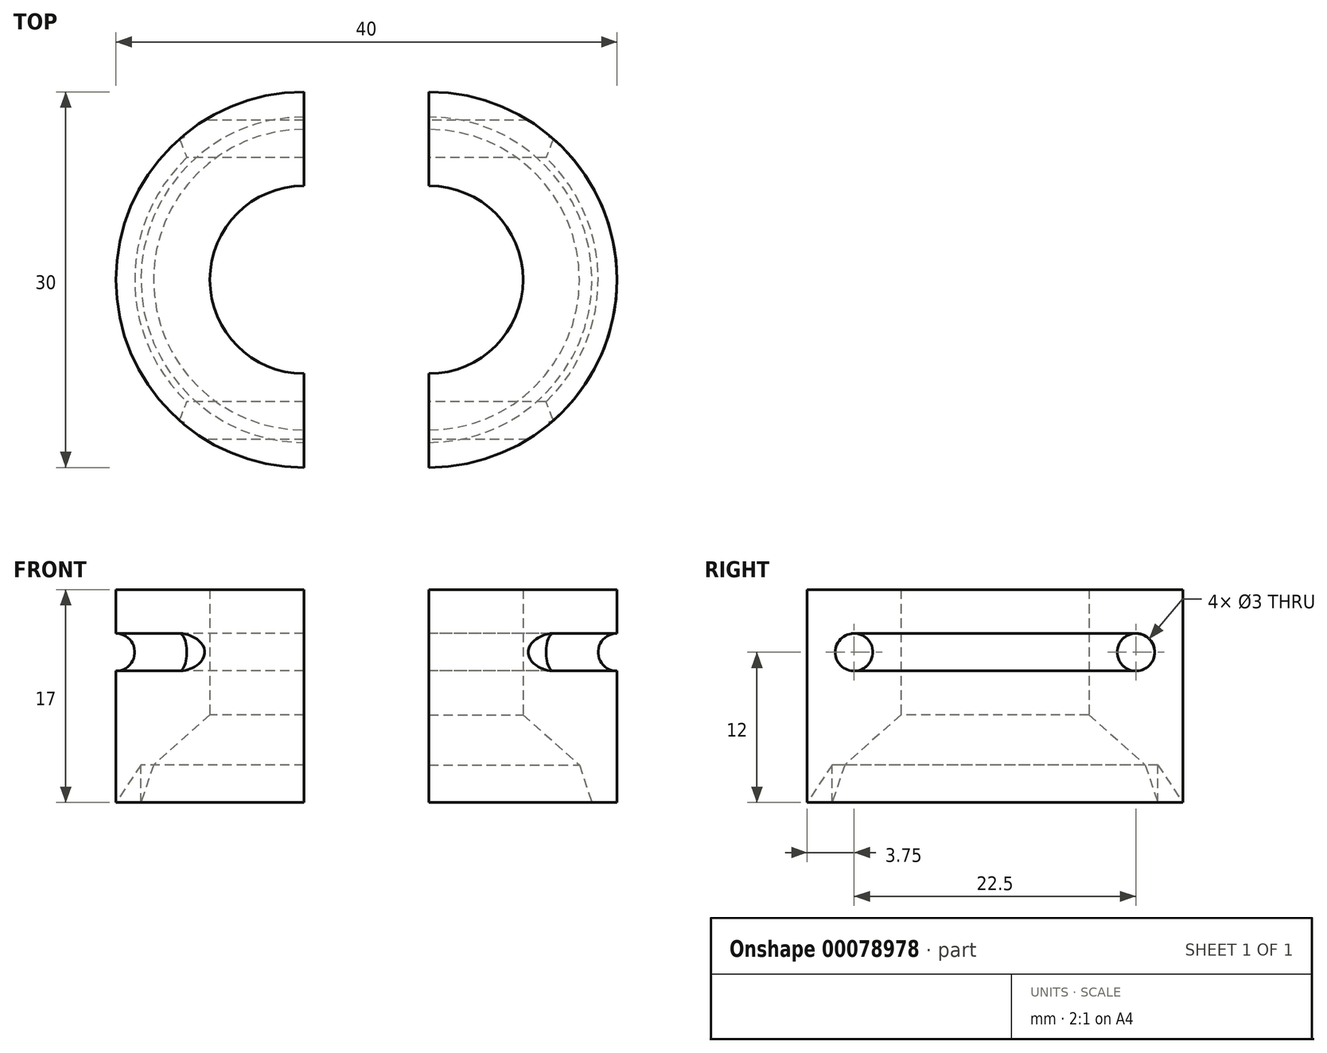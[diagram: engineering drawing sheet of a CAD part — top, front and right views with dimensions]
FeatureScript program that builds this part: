
annotation { "Feature Type Name" : "Feature", "Feature Type Description" : "" }
export const myFeature = defineFeature(function(context is Context, id is Id, definition is map)
    precondition{}
    {
        {
            var Q0;
            Q0=qCreatedBy(makeId("Top.planeOp"),FACE);
            var sketch = newSketch(context, id + "F0", { "sketchPlane" : qUnion([Q0])});
            skLineSegment(sketch, "E0", {"start": v(-10, 15) * mm, "end": v(-10, -15) * mm});
            skLineSegment(sketch, "E1", {"start": v(0, 15) * mm, "end": v(0, -15) * mm});
            skArc(sketch, "E2", {"start": v(-10, 15) * mm, "mid": v(-25, 0) * mm, "end": v(-10, -15) * mm});
            skArc(sketch, "E3", {"start": v(0, -15) * mm, "mid": v(15, 0) * mm, "end": v(0, 15) * mm});
            skArc(sketch, "E4", {"start": v(-10, 13) * mm, "mid": v(-23, 0) * mm, "end": v(-10, -13) * mm});
            skArc(sketch, "E5", {"start": v(0, -13) * mm, "mid": v(13, 0) * mm, "end": v(0, 13) * mm});
            skArc(sketch, "E6", {"start": v(0, -7.5) * mm, "mid": v(7.5, 0) * mm, "end": v(0, 7.5) * mm});
            skArc(sketch, "E7", {"start": v(-10, 7.5) * mm, "mid": v(-17.5, 0) * mm, "end": v(-10, -7.5) * mm});
            skArc(sketch, "E8", {"start": v(-10, 12) * mm, "mid": v(-22, 0) * mm, "end": v(-10, -12) * mm});
            skArc(sketch, "E9", {"start": v(0, -12) * mm, "mid": v(12, 0) * mm, "end": v(0, 12) * mm});
            skSolve(sketch);
        }
        {
            var Q0;
            {var subQ0=sQuery(id+"F0.wireOp",EDGE,"E4");Q0=makeQuery(id+"F0.imprint","IMPRINT",FACE,{"disambiguationData":[TD([[makeQuery(id+"F0.imprint","IMPRINT",EDGE,{"derivedFrom":subQ0}),1.0]])]});}
            var Q1;
            {var subQ0=sQuery(id+"F0.wireOp",EDGE,"E5");Q1=makeQuery(id+"F0.imprint","IMPRINT",FACE,{"disambiguationData":[TD([[makeQuery(id+"F0.imprint","IMPRINT",EDGE,{"derivedFrom":subQ0}),1.0]])]});}
            var Q2;
            {var subQ0=sQuery(id+"F0.wireOp",EDGE,"E7");Q2=makeQuery(id+"F0.imprint","IMPRINT",FACE,{"disambiguationData":[TD([[makeQuery(id+"F0.imprint","IMPRINT",EDGE,{"derivedFrom":subQ0}),-1.0]])]});}
            var Q3;
            {var subQ0=sQuery(id+"F0.wireOp",EDGE,"E6");Q3=makeQuery(id+"F0.imprint","IMPRINT",FACE,{"disambiguationData":[TD([[makeQuery(id+"F0.imprint","IMPRINT",EDGE,{"derivedFrom":subQ0}),-1.0]])]});}
            var Q4;
            {var subQ0=sQuery(id+"F0.wireOp",EDGE,"E2");Q4=makeQuery(id+"F0.imprint","IMPRINT",FACE,{"disambiguationData":[TD([[makeQuery(id+"F0.imprint","IMPRINT",EDGE,{"derivedFrom":subQ0}),1.0]])]});}
            var Q5;
            {var subQ0=sQuery(id+"F0.wireOp",EDGE,"E3");Q5=makeQuery(id+"F0.imprint","IMPRINT",FACE,{"disambiguationData":[TD([[makeQuery(id+"F0.imprint","IMPRINT",EDGE,{"derivedFrom":subQ0}),1.0]])]});}
            extrude(context, id + "F1", {"entities" : qUnion([Q0, Q1, Q2, Q3, Q4, Q5]), "depth" : 10 * mm});
        }
        {
            var Q0;
            {var subQ0=sQuery(id+"F0.wireOp",EDGE,"E1");var subQ2=makeQuery(id+"F0.imprint","INTERSECT",VERTEX,{"disambiguationData":[OD(1.0)],"derivedFrom":[subQ0,sQuery(id+"F0.wireOp",EDGE,"E5")]});Q0=makeQuery(id+"F1.opExtrude","SWEPT_FACE",FACE,{"disambiguationData":[OSD([subQ0]),TDD([makeQuery(id+"F0.imprint","IMPRINT",EDGE,{"disambiguationData":[TD([[makeQuery(id+"F0.imprint","INTERSECT",VERTEX,{"disambiguationData":[OD(0.0)],"derivedFrom":[subQ0,sQuery(id+"F0.wireOp",EDGE,"E3")]}),-1.0]])],"derivedFrom":subQ0}),makeQuery(id+"F0.imprint","IMPRINT",EDGE,{"disambiguationData":[TD([[subQ2,-1.0]])],"derivedFrom":subQ0}),makeQuery(id+"F0.imprint","IMPRINT",EDGE,{"disambiguationData":[TD([[makeQuery(id+"F0.imprint","INTERSECT",VERTEX,{"disambiguationData":[OD(1.0)],"derivedFrom":[subQ0,sQuery(id+"F0.wireOp",EDGE,"E6")]}),1.0]])],"derivedFrom":subQ0})])]});}
            var sketch = newSketch(context, id + "F2", { "sketchPlane" : qUnion([Q0])});
            skLineSegment(sketch, "E10", {"start": v(-11.25, 10) * mm, "end": v(-11.25, 0) * mm, "construction": true});
            skLineSegment(sketch, "E11", {"start": v(-15, 5) * mm, "end": v(-7.5, 5) * mm, "construction": true});
            skSolve(sketch);
        }
        {
            var Q0;
            {var subQ0=sQuery(id+"F0.wireOp",EDGE,"E1");var subQ1=makeQuery(id+"F0.imprint","INTERSECT",VERTEX,{"disambiguationData":[OD(0.0)],"derivedFrom":[subQ0,sQuery(id+"F0.wireOp",EDGE,"E5")]});Q0=makeQuery(id+"F1.opExtrude","SWEPT_FACE",FACE,{"disambiguationData":[OSD([subQ0]),TDD([makeQuery(id+"F0.imprint","IMPRINT",EDGE,{"disambiguationData":[TD([[makeQuery(id+"F0.imprint","INTERSECT",VERTEX,{"disambiguationData":[OD(0.0)],"derivedFrom":[subQ0,sQuery(id+"F0.wireOp",EDGE,"E6")]}),-1.0]])],"derivedFrom":subQ0}),makeQuery(id+"F0.imprint","IMPRINT",EDGE,{"disambiguationData":[TD([[subQ1,1.0]])],"derivedFrom":subQ0}),makeQuery(id+"F0.imprint","IMPRINT",EDGE,{"disambiguationData":[TD([[makeQuery(id+"F0.imprint","INTERSECT",VERTEX,{"disambiguationData":[OD(1.0)],"derivedFrom":[subQ0,sQuery(id+"F0.wireOp",EDGE,"E3")]}),1.0]])],"derivedFrom":subQ0})])]});}
            var sketch = newSketch(context, id + "F3", { "sketchPlane" : qUnion([Q0])});
            skLineSegment(sketch, "E12", {"start": v(11.25, 10) * mm, "end": v(11.25, 0) * mm, "construction": true});
            skLineSegment(sketch, "E13", {"start": v(15, 5) * mm, "end": v(7.5, 5) * mm, "construction": true});
            skCircle(sketch, "E14", {"center": v(11.25, 5) * mm, "radius": 1.5 * mm});
            skCircle(sketch, "E15", {"center": v(-11.25, 5) * mm, "radius": 1.5 * mm});
            skCircle(sketch, "E16", {"center": v(15, 5) * mm, "radius": 1.5 * mm});
            skLineSegment(sketch, "E17", {"start": v(0, 0) * mm, "end": v(0, 8.48) * mm, "construction": true});
            skSolve(sketch);
        }
        {
            var Q0;
            Q0=makeQuery(id+"F3.imprint","IMPRINT",FACE,{"disambiguationData":[TD([[makeQuery(id+"F3.imprint","IMPRINT",EDGE,{"derivedFrom":sQuery(id+"F3.wireOp",EDGE,"E15")}),1.0]])]});
            var Q1;
            Q1=makeQuery(id+"F3.imprint","IMPRINT",FACE,{"disambiguationData":[TD([[makeQuery(id+"F3.imprint","IMPRINT",EDGE,{"derivedFrom":sQuery(id+"F3.wireOp",EDGE,"E14")}),1.0]])]});
            extrude(context, id + "F4", {"entities" : qUnion([Q0, Q1]), "operationType" : NewBodyOperationType.REMOVE, "endBound" : BoundingType.SYMMETRIC, "oppositeDirection" : true, "depth" : 50 * mm});
        }
        {
            var Q0;
            {var subQ0=sQuery(id+"F3.wireOp",EDGE,"E16");var subQ1=sQuery(id+"F0.wireOp",EDGE,"E3");var subQ2=sQuery(id+"F0.wireOp",EDGE,"E1");var subQ3=makeQuery(id+"F1.opExtrude","SWEPT_EDGE",EDGE,{"disambiguationData":[OSD([subQ2,subQ1]),TDD([makeQuery(id+"F0.imprint","INTERSECT",VERTEX,{"disambiguationData":[OD(1.0)],"derivedFrom":[subQ2,subQ1]})])]});var subQ4=makeQuery(id+"F3.imprint","INTERSECT",VERTEX,{"disambiguationData":[OD(0.0)],"derivedFrom":[subQ3,subQ0]});Q0=makeQuery(id+"F3.imprint","IMPRINT",FACE,{"disambiguationData":[TD([[makeQuery(id+"F3.imprint","IMPRINT",EDGE,{"disambiguationData":[TD([[subQ4,1.0]])],"derivedFrom":subQ0}),1.0]])]});}
            var Q1;
            Q1=sQuery(id+"F3.wireOp",EDGE,"E17");
            revolve(context, id + "F5", {"operationType" : NewBodyOperationType.REMOVE, "entities" : qUnion([Q0]), "axis" : qUnion([Q1]), "revolveType" : RevolveType.TWO_DIRECTIONS, "angle" : 140 * degree, "angleBack" : 40 * degree});
        }
        {
            var Q0;
            {var subQ0=sQuery(id+"F0.wireOp",EDGE,"E0");var subQ1=makeQuery(id+"F0.imprint","INTERSECT",VERTEX,{"disambiguationData":[OD(1.0)],"derivedFrom":[subQ0,sQuery(id+"F0.wireOp",EDGE,"E4")]});Q0=makeQuery(id+"F1.opExtrude","SWEPT_FACE",FACE,{"disambiguationData":[OSD([subQ0]),TDD([makeQuery(id+"F0.imprint","IMPRINT",EDGE,{"disambiguationData":[TD([[makeQuery(id+"F0.imprint","INTERSECT",VERTEX,{"disambiguationData":[OD(1.0)],"derivedFrom":[subQ0,sQuery(id+"F0.wireOp",EDGE,"E7")]}),-1.0]])],"derivedFrom":subQ0}),makeQuery(id+"F0.imprint","IMPRINT",EDGE,{"disambiguationData":[TD([[subQ1,1.0]])],"derivedFrom":subQ0}),makeQuery(id+"F0.imprint","IMPRINT",EDGE,{"disambiguationData":[TD([[makeQuery(id+"F0.imprint","INTERSECT",VERTEX,{"disambiguationData":[OD(1.0)],"derivedFrom":[subQ0,sQuery(id+"F0.wireOp",EDGE,"E2")]}),1.0]])],"derivedFrom":subQ0})])]});}
            var sketch = newSketch(context, id + "F6", { "sketchPlane" : qUnion([Q0])});
            skCircle(sketch, "E18", {"center": v(-15, 5) * mm, "radius": 1.5 * mm});
            skLineSegment(sketch, "E19", {"start": v(0, 0) * mm, "end": v(0, 13.63) * mm, "construction": true});
            skSolve(sketch);
        }
        {
            var Q0;
            {var subQ0=sQuery(id+"F6.wireOp",EDGE,"E18");var subQ1=sQuery(id+"F0.wireOp",EDGE,"E2");var subQ2=sQuery(id+"F0.wireOp",EDGE,"E0");var subQ3=makeQuery(id+"F1.opExtrude","SWEPT_EDGE",EDGE,{"disambiguationData":[OSD([subQ2,subQ1]),TDD([makeQuery(id+"F0.imprint","INTERSECT",VERTEX,{"disambiguationData":[OD(1.0)],"derivedFrom":[subQ2,subQ1]})])]});var subQ4=makeQuery(id+"F6.imprint","INTERSECT",VERTEX,{"disambiguationData":[OD(0.0)],"derivedFrom":[subQ3,subQ0]});Q0=makeQuery(id+"F6.imprint","IMPRINT",FACE,{"disambiguationData":[TD([[makeQuery(id+"F6.imprint","IMPRINT",EDGE,{"disambiguationData":[TD([[subQ4,-1.0]])],"derivedFrom":subQ0}),1.0]])]});}
            var Q1;
            Q1=sQuery(id+"F6.wireOp",EDGE,"E19");
            revolve(context, id + "F7", {"operationType" : NewBodyOperationType.REMOVE, "entities" : qUnion([Q0]), "axis" : qUnion([Q1]), "revolveType" : RevolveType.TWO_DIRECTIONS, "angle" : 320 * degree, "angleBack" : 220 * degree});
        }
        {
            var Q0;
            {var subQ0=sQuery(id+"F0.wireOp",EDGE,"E3");Q0=makeQuery(id+"F0.imprint","IMPRINT",FACE,{"disambiguationData":[TD([[makeQuery(id+"F0.imprint","IMPRINT",EDGE,{"derivedFrom":subQ0}),1.0]])]});}
            var Q1;
            {var subQ0=sQuery(id+"F0.wireOp",EDGE,"E2");Q1=makeQuery(id+"F0.imprint","IMPRINT",FACE,{"disambiguationData":[TD([[makeQuery(id+"F0.imprint","IMPRINT",EDGE,{"derivedFrom":subQ0}),1.0]])]});}
            extrude(context, id + "F8", {"entities" : qUnion([Q0, Q1]), "operationType" : NewBodyOperationType.ADD, "oppositeDirection" : true, "depth" : 7 * mm});
        }
        {
            var Q0;
            {var subQ0=sQuery(id+"F0.wireOp",EDGE,"E5");Q0=makeQuery(id+"F0.imprint","IMPRINT",FACE,{"disambiguationData":[TD([[makeQuery(id+"F0.imprint","IMPRINT",EDGE,{"derivedFrom":subQ0}),1.0]])]});}
            var Q1;
            {var subQ0=sQuery(id+"F0.wireOp",EDGE,"E4");Q1=makeQuery(id+"F0.imprint","IMPRINT",FACE,{"disambiguationData":[TD([[makeQuery(id+"F0.imprint","IMPRINT",EDGE,{"derivedFrom":subQ0}),1.0]])]});}
            extrude(context, id + "F9", {"entities" : qUnion([Q0, Q1]), "operationType" : NewBodyOperationType.ADD, "oppositeDirection" : true, "depth" : 4 * mm});
        }
        {
            var Q0;
            {var subQ0=sQuery(id+"F0.wireOp",EDGE,"E6");Q0=makeQuery(id+"F0.imprint","IMPRINT",FACE,{"disambiguationData":[TD([[makeQuery(id+"F0.imprint","IMPRINT",EDGE,{"derivedFrom":subQ0}),-1.0]])]});}
            var Q1;
            Q1=makeQuery(id+"F9.opExtrude","CAP_FACE",FACE,{"disambiguationData":[OSD([sQuery(id+"F0.wireOp",EDGE,"E1"),sQuery(id+"F0.wireOp",EDGE,"E5"),sQuery(id+"F0.wireOp",EDGE,"E9")])],"isStart":false});
            loft(context, id + "F10", {"operationType" : NewBodyOperationType.ADD, "sheetProfilesArray" : [{ "sheetProfileEntities" : qUnion([Q0]) }, { "sheetProfileEntities" : qUnion([Q1]) }]});
        }
        {
            var Q0;
            {var subQ0=sQuery(id+"F0.wireOp",EDGE,"E7");Q0=makeQuery(id+"F0.imprint","IMPRINT",FACE,{"disambiguationData":[TD([[makeQuery(id+"F0.imprint","IMPRINT",EDGE,{"derivedFrom":subQ0}),-1.0]])]});}
            var Q1;
            Q1=makeQuery(id+"F9.opExtrude","CAP_FACE",FACE,{"disambiguationData":[OSD([sQuery(id+"F0.wireOp",EDGE,"E0"),sQuery(id+"F0.wireOp",EDGE,"E4"),sQuery(id+"F0.wireOp",EDGE,"E8")])],"isStart":false});
            loft(context, id + "F11", {"operationType" : NewBodyOperationType.ADD, "sheetProfilesArray" : [{ "sheetProfileEntities" : qUnion([Q0]) }, { "sheetProfileEntities" : qUnion([Q1]) }]});
        }
        {
            var Q0;
            Q0=makeQuery(id+"F9.opExtrude","CAP_FACE",FACE,{"disambiguationData":[OSD([sQuery(id+"F0.wireOp",EDGE,"E1"),sQuery(id+"F0.wireOp",EDGE,"E5"),sQuery(id+"F0.wireOp",EDGE,"E9")])],"isStart":false});
            var Q1;
            Q1=makeQuery(id+"F8.opExtrude","CAP_FACE",FACE,{"disambiguationData":[OSD([sQuery(id+"F0.wireOp",EDGE,"E1"),sQuery(id+"F0.wireOp",EDGE,"E3"),sQuery(id+"F0.wireOp",EDGE,"E5")])],"isStart":false});
            loft(context, id + "F12", {"operationType" : NewBodyOperationType.ADD, "sheetProfilesArray" : [{ "sheetProfileEntities" : qUnion([Q0]) }, { "sheetProfileEntities" : qUnion([Q1]) }]});
        }
        {
            var Q0;
            Q0=makeQuery(id+"F9.opExtrude","CAP_FACE",FACE,{"disambiguationData":[OSD([sQuery(id+"F0.wireOp",EDGE,"E0"),sQuery(id+"F0.wireOp",EDGE,"E4"),sQuery(id+"F0.wireOp",EDGE,"E8")])],"isStart":false});
            var Q1;
            Q1=makeQuery(id+"F8.opExtrude","CAP_FACE",FACE,{"disambiguationData":[OSD([sQuery(id+"F0.wireOp",EDGE,"E0"),sQuery(id+"F0.wireOp",EDGE,"E2"),sQuery(id+"F0.wireOp",EDGE,"E4")])],"isStart":false});
            loft(context, id + "F13", {"sheetProfilesArray" : [{ "sheetProfileEntities" : qUnion([Q0]) }, { "sheetProfileEntities" : qUnion([Q1]) }]});
        }
    });
